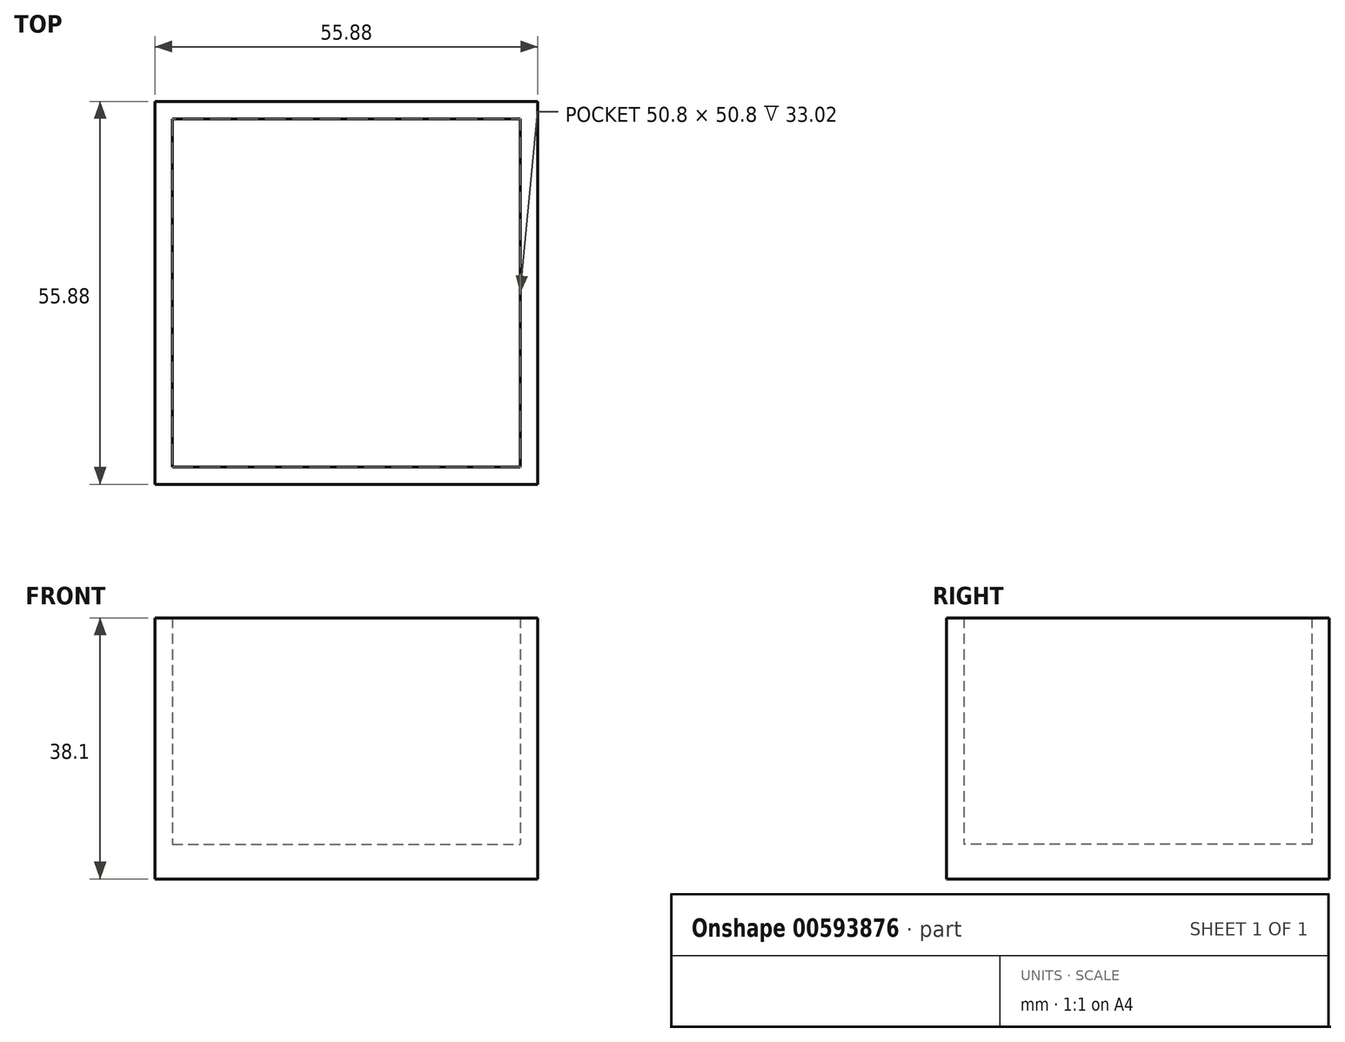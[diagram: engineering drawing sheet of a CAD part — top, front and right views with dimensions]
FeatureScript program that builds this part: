
annotation { "Feature Type Name" : "Feature", "Feature Type Description" : "" }
export const myFeature = defineFeature(function(context is Context, id is Id, definition is map)
    precondition{}
    {
        {
            var Q0;
            Q0=qCreatedBy(makeId("Top.planeOp"),FACE);
            var sketch = newSketch(context, id + "F0", { "sketchPlane" : qUnion([Q0])});
            skLineSegment(sketch, "E0.bottom", {"start": v(25.4, -25.4) * mm, "end": v(-25.4, -25.4) * mm});
            skLineSegment(sketch, "E0.top", {"start": v(25.4, 25.4) * mm, "end": v(-25.4, 25.4) * mm});
            skLineSegment(sketch, "E0.left", {"start": v(25.4, -25.4) * mm, "end": v(25.4, 25.4) * mm});
            skLineSegment(sketch, "E0.right", {"start": v(-25.4, -25.4) * mm, "end": v(-25.4, 25.4) * mm});
            skPoint(sketch, "E0.middle", {"position": v(0, 0) * mm});
            skLineSegment(sketch, "E1.0", {"start": v(27.94, 27.94) * mm, "end": v(-27.94, 27.94) * mm});
            skLineSegment(sketch, "E1.1", {"start": v(27.94, -27.94) * mm, "end": v(27.94, 27.94) * mm});
            skLineSegment(sketch, "E1.2", {"start": v(27.94, -27.94) * mm, "end": v(-27.94, -27.94) * mm});
            skLineSegment(sketch, "E1.3", {"start": v(-27.94, -27.94) * mm, "end": v(-27.94, 27.94) * mm});
            skSolve(sketch);
        }
        {
            var Q0;
            Q0 = qSketchRegion(id + "F0", true);
            var Q1;
            Q1=makeQuery(id+"F0.imprint","IMPRINT",FACE,{"disambiguationData":[TD([[makeQuery(id+"F0.imprint","IMPRINT",EDGE,{"derivedFrom":sQuery(id+"F0.wireOp",EDGE,"E0.bottom")}),-1.0]])]});
            extrude(context, id + "F1", {"entities" : qUnion([Q0, Q1]), "depth" : 5.08 * mm, "offsetDistance" : 25.4 * mm});
        }
        {
            var Q0;
            Q0=makeQuery(id+"F0.imprint","IMPRINT",FACE,{"disambiguationData":[TD([[makeQuery(id+"F0.imprint","IMPRINT",EDGE,{"derivedFrom":sQuery(id+"F0.wireOp",EDGE,"E0.bottom")}),1.0]])]});
            extrude(context, id + "F2", {"entities" : qUnion([Q0]), "operationType" : NewBodyOperationType.ADD, "depth" : 38.1 * mm, "offsetDistance" : 25.4 * mm});
        }
    });
